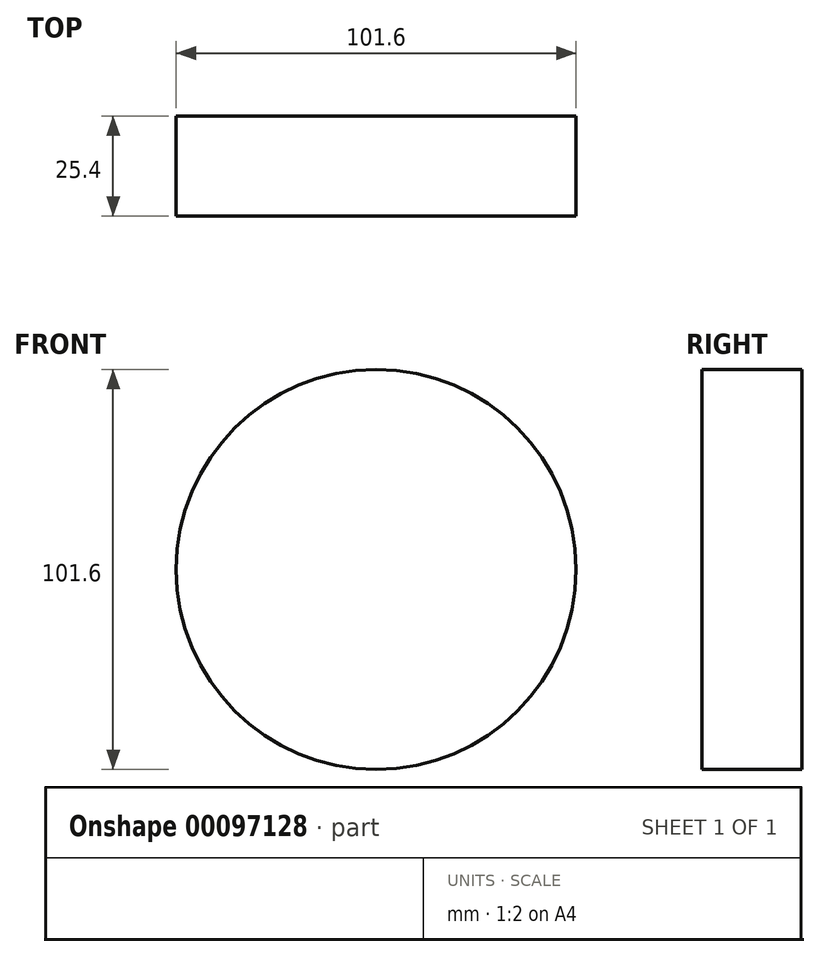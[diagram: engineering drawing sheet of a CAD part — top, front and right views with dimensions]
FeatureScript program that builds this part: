
annotation { "Feature Type Name" : "Feature", "Feature Type Description" : "" }
export const myFeature = defineFeature(function(context is Context, id is Id, definition is map)
    precondition{}
    {
        {
            var Q0;
            Q0=qCreatedBy(makeId("Front.planeOp"),FACE);
            var sketch = newSketch(context, id + "F0", { "sketchPlane" : qUnion([Q0])});
            skCircle(sketch, "E0", {"center": v(0, 0) * mm, "radius": 50.8 * mm});
            skSolve(sketch);
        }
        {
            var Q0;
            Q0=makeQuery(id+"F0.imprint","IMPRINT",FACE,{"disambiguationData":[TD([[makeQuery(id+"F0.imprint","IMPRINT",EDGE,{"derivedFrom":sQuery(id+"F0.wireOp",EDGE,"E0")}),1.0]])]});
            extrude(context, id + "F1", {"entities" : qUnion([Q0]), "depth" : 25.4 * mm});
        }
    });
